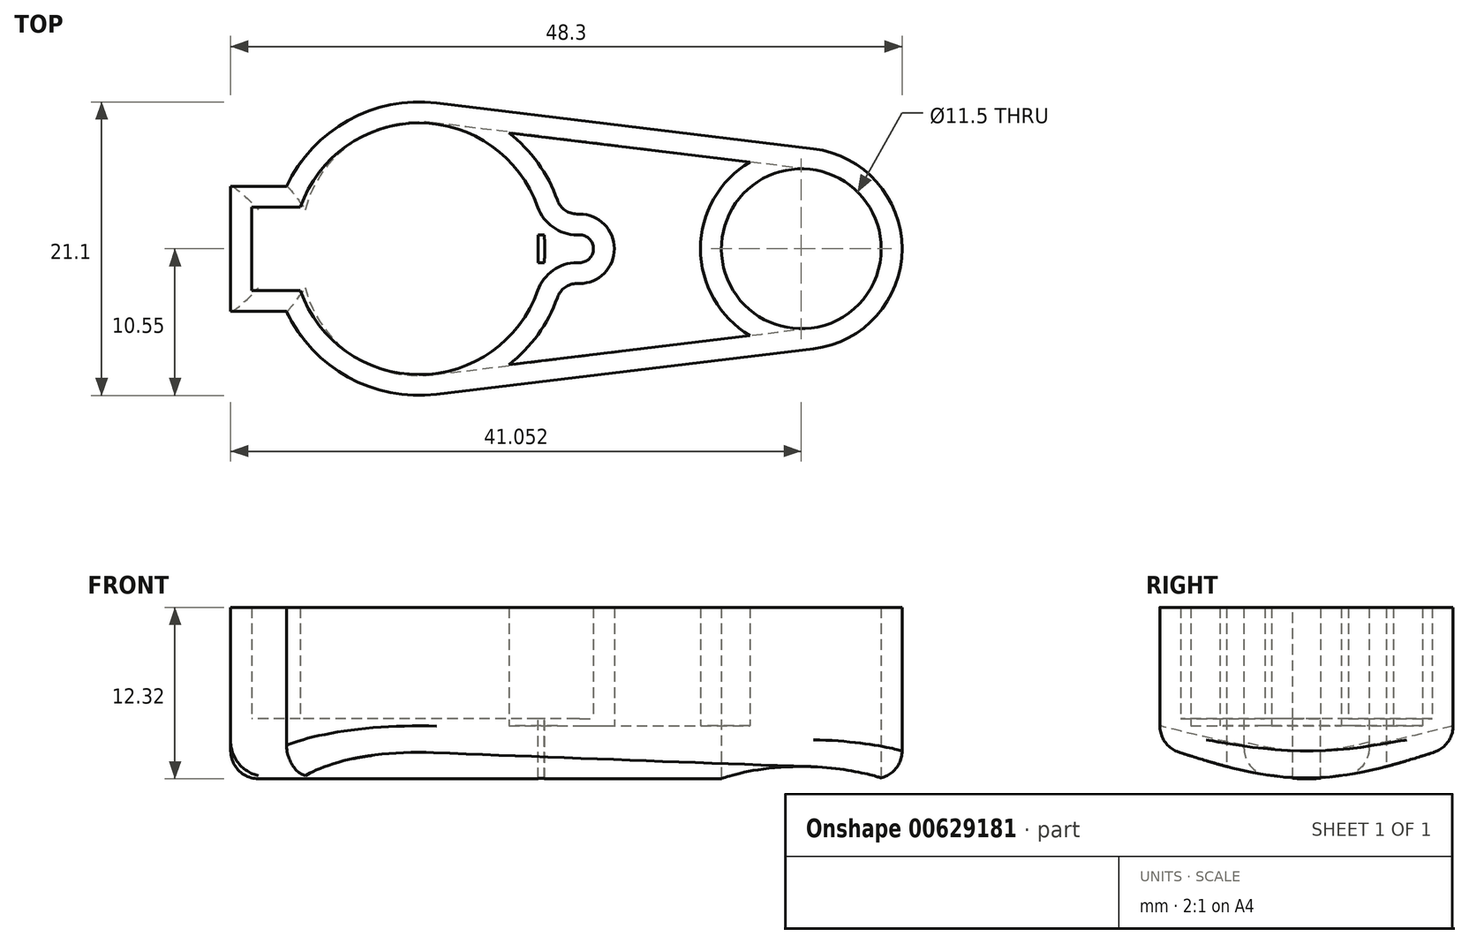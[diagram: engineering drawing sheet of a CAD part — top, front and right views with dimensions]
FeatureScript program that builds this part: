
annotation { "Feature Type Name" : "Feature", "Feature Type Description" : "" }
export const myFeature = defineFeature(function(context is Context, id is Id, definition is map)
    precondition{}
    {
        {
            var Q0;
            Q0=qCreatedBy(makeId("Top.planeOp"),FACE);
            var sketch = newSketch(context, id + "F0", { "sketchPlane" : qUnion([Q0])});
            skCircle(sketch, "E0", {"center": v(1.2, 0) * mm, "radius": 7.25 * mm});
            skCircle(sketch, "E1", {"center": v(-26.3, 0) * mm, "radius": 10.55 * mm});
            skLineSegment(sketch, "E2", {"start": v(-25.03, 10.47) * mm, "end": v(2.07, 7.2) * mm});
            skLineSegment(sketch, "E3", {"start": v(-25.03, -10.47) * mm, "end": v(2.07, -7.2) * mm});
            skCircle(sketch, "E4", {"center": v(-26.3, 0) * mm, "radius": 9.05 * mm});
            skCircle(sketch, "E5", {"center": v(1.2, 0) * mm, "radius": 5.75 * mm});
            skPoint(sketch, "E6", {"position": v(-35.35, 0) * mm});
            skPoint(sketch, "E7", {"position": v(6.95, 0) * mm});
            skLineSegment(sketch, "E8", {"start": v(-34.84, 3) * mm, "end": v(-34.84, -3) * mm});
            skLineSegment(sketch, "E9.bottom", {"start": v(-34.84, 3) * mm, "end": v(-38.35, 3) * mm});
            skLineSegment(sketch, "E9.top", {"start": v(-34.84, -3) * mm, "end": v(-38.35, -3) * mm});
            skLineSegment(sketch, "E9.right", {"start": v(-38.35, 3) * mm, "end": v(-38.35, -3) * mm});
            skLineSegment(sketch, "E10.0", {"start": v(-35.28, -4.5) * mm, "end": v(-39.85, -4.5) * mm});
            skLineSegment(sketch, "E10.1", {"start": v(-39.85, 4.5) * mm, "end": v(-39.85, -4.5) * mm});
            skLineSegment(sketch, "E10.2", {"start": v(-35.28, 4.5) * mm, "end": v(-39.85, 4.5) * mm});
            skPoint(sketch, "E11", {"position": v(-15.75, 0) * mm});
            skLineSegment(sketch, "E12.bottom", {"start": v(-13.75, 1) * mm, "end": v(-17.75, 1) * mm});
            skLineSegment(sketch, "E12.top", {"start": v(-13.75, -1) * mm, "end": v(-17.75, -1) * mm});
            skLineSegment(sketch, "E12.left", {"start": v(-13.75, 1) * mm, "end": v(-13.75, -1) * mm});
            skLineSegment(sketch, "E12.right", {"start": v(-17.75, 1) * mm, "end": v(-17.75, -1) * mm});
            skLineSegment(sketch, "E13", {"start": v(-17.3, 1) * mm, "end": v(-17.75, 1) * mm});
            skLineSegment(sketch, "E14", {"start": v(-17.3, -1) * mm, "end": v(-17.75, -1) * mm});
            skSolve(sketch);
        }
        {
            var Q0;
            {var subQ0=sQuery(id+"F0.wireOp",EDGE,"E2");Q0=makeQuery(id+"F0.imprint","IMPRINT",FACE,{"disambiguationData":[TD([[makeQuery(id+"F0.imprint","IMPRINT",EDGE,{"derivedFrom":subQ0}),-1.0]])]});}
            var Q1;
            Q1=makeQuery(id+"F0.imprint","IMPRINT",FACE,{"disambiguationData":[TD([[makeQuery(id+"F0.imprint","IMPRINT",EDGE,{"derivedFrom":sQuery(id+"F0.wireOp",EDGE,"E5")}),-1.0]])]});
            var Q2;
            {var subQ0=sQuery(id+"F0.wireOp",EDGE,"E1");var subQ8=makeQuery(id+"F0.imprint","INTERSECT",VERTEX,{"derivedFrom":[subQ0,sQuery(id+"F0.wireOp",EDGE,"E2")]});Q2=makeQuery(id+"F0.imprint","IMPRINT",FACE,{"disambiguationData":[TD([[makeQuery(id+"F0.imprint","IMPRINT",EDGE,{"disambiguationData":[TD([[subQ8,-1.0]])],"derivedFrom":subQ0}),1.0]])]});}
            var Q3;
            {var subQ0=sQuery(id+"F0.wireOp",EDGE,"E9.right");Q3=makeQuery(id+"F0.imprint","IMPRINT",FACE,{"disambiguationData":[TD([[makeQuery(id+"F0.imprint","IMPRINT",EDGE,{"derivedFrom":subQ0}),-1.0]])]});}
            var Q4;
            {var subQ5=sQuery(id+"F0.wireOp",EDGE,"E1");var subQ9=makeQuery(id+"F0.imprint","INTERSECT",VERTEX,{"derivedFrom":[subQ5,sQuery(id+"F0.wireOp",EDGE,"E10.0")]});Q4=makeQuery(id+"F0.imprint","IMPRINT",FACE,{"disambiguationData":[TD([[makeQuery(id+"F0.imprint","IMPRINT",EDGE,{"disambiguationData":[TD([[subQ9,1.0]])],"derivedFrom":subQ5}),1.0]])]});}
            extrude(context, id + "F1", {"entities" : qUnion([Q0, Q1, Q2, Q3, Q4]), "depth" : 8 * mm, "offsetDistance" : 25 * mm});
        }
        {
            var Q0;
            Q0=makeQuery(id+"F1.opExtrude","SWEPT_EDGE",EDGE,{"disambiguationData":[OSD([sQuery(id+"F0.wireOp",EDGE,"E12.bottom"),sQuery(id+"F0.wireOp",EDGE,"E12.left")])]});
            var Q1;
            Q1=makeQuery(id+"F1.opExtrude","SWEPT_EDGE",EDGE,{"disambiguationData":[OSD([sQuery(id+"F0.wireOp",EDGE,"E12.top"),sQuery(id+"F0.wireOp",EDGE,"E12.left")])]});
            fillet(context, id + "F2", {"entities" : qUnion([Q0, Q1]), "radius" : 1 * mm, "tangentPropagation" : true, "allowEdgeOverflow" : false});
        }
        {
            var Q0;
            Q0=makeQuery(id+"F1.opExtrude","SWEPT_EDGE",EDGE,{"disambiguationData":[OSD([sQuery(id+"F0.wireOp",EDGE,"E4"),sQuery(id+"F0.wireOp",EDGE,"E13")])]});
            var Q1;
            Q1=makeQuery(id+"F1.opExtrude","SWEPT_EDGE",EDGE,{"disambiguationData":[OSD([sQuery(id+"F0.wireOp",EDGE,"E4"),sQuery(id+"F0.wireOp",EDGE,"E14")])]});
            fillet(context, id + "F3", {"entities" : qUnion([Q0, Q1]), "radius" : 3 * mm, "tangentPropagation" : true, "allowEdgeOverflow" : false});
        }
        {
            var Q0;
            Q0=makeQuery(id+"F1.opExtrude","CAP_FACE",FACE,{"disambiguationData":[OSD([sQuery(id+"F0.wireOp",EDGE,"E0"),sQuery(id+"F0.wireOp",EDGE,"E1"),sQuery(id+"F0.wireOp",EDGE,"E2"),sQuery(id+"F0.wireOp",EDGE,"E3"),sQuery(id+"F0.wireOp",EDGE,"E4"),sQuery(id+"F0.wireOp",EDGE,"E5"),sQuery(id+"F0.wireOp",EDGE,"E9.bottom"),sQuery(id+"F0.wireOp",EDGE,"E9.top"),sQuery(id+"F0.wireOp",EDGE,"E9.right"),sQuery(id+"F0.wireOp",EDGE,"E10.0"),sQuery(id+"F0.wireOp",EDGE,"E10.1"),sQuery(id+"F0.wireOp",EDGE,"E10.2"),sQuery(id+"F0.wireOp",EDGE,"E12.bottom"),sQuery(id+"F0.wireOp",EDGE,"E12.top"),sQuery(id+"F0.wireOp",EDGE,"E12.left"),sQuery(id+"F0.wireOp",EDGE,"E13"),sQuery(id+"F0.wireOp",EDGE,"E14")])],"isStart":true});
            var Q1;
            {var subQ3=sQuery(id+"F0.wireOp",EDGE,"E8");Q1=makeQuery(id+"F0.imprint","IMPRINT",FACE,{"disambiguationData":[TD([[makeQuery(id+"F0.imprint","IMPRINT",EDGE,{"derivedFrom":subQ3}),1.0]])]});}
            var Q2;
            {var subQ0=sQuery(id+"F0.wireOp",EDGE,"E9.bottom");var subQ1=sQuery(id+"F0.wireOp",EDGE,"E1");var subQ2=makeQuery(id+"F0.imprint","INTERSECT",VERTEX,{"derivedFrom":[subQ1,subQ0]});Q2=makeQuery(id+"F0.imprint","IMPRINT",FACE,{"disambiguationData":[TD([[makeQuery(id+"F0.imprint","IMPRINT",EDGE,{"disambiguationData":[TD([[subQ2,-1.0]])],"derivedFrom":subQ1}),1.0]])]});}
            var Q3;
            {var subQ5=sQuery(id+"F0.wireOp",EDGE,"E9.right");Q3=makeQuery(id+"F0.imprint","IMPRINT",FACE,{"disambiguationData":[TD([[makeQuery(id+"F0.imprint","IMPRINT",EDGE,{"derivedFrom":subQ5}),1.0]])]});}
            var Q4;
            {var subQ5=sQuery(id+"F0.wireOp",EDGE,"E12.left");Q4=makeQuery(id+"F0.imprint","IMPRINT",FACE,{"disambiguationData":[TD([[makeQuery(id+"F0.imprint","IMPRINT",EDGE,{"derivedFrom":subQ5}),-1.0]])]});}
            var Q5;
            {var subQ1=sQuery(id+"F0.wireOp",EDGE,"E12.bottom");var subQ6=sQuery(id+"F0.wireOp",EDGE,"E1");var subQ8=makeQuery(id+"F0.imprint","INTERSECT",VERTEX,{"derivedFrom":[subQ6,subQ1]});Q5=makeQuery(id+"F0.imprint","IMPRINT",FACE,{"disambiguationData":[TD([[makeQuery(id+"F0.imprint","IMPRINT",EDGE,{"disambiguationData":[TD([[subQ8,1.0]])],"derivedFrom":subQ6}),1.0]])]});}
            var Q6;
            {var subQ3=sQuery(id+"F0.wireOp",EDGE,"E14");Q6=makeQuery(id+"F0.imprint","IMPRINT",FACE,{"disambiguationData":[TD([[makeQuery(id+"F0.imprint","IMPRINT",EDGE,{"derivedFrom":subQ3}),1.0]])]});}
            var Q7;
            {var subQ0=sQuery(id+"F0.wireOp",EDGE,"E8");Q7=makeQuery(id+"F0.imprint","IMPRINT",FACE,{"disambiguationData":[TD([[makeQuery(id+"F0.imprint","IMPRINT",EDGE,{"derivedFrom":subQ0}),-1.0]])]});}
            var Q8;
            {var subQ6=sQuery(id+"F0.wireOp",EDGE,"E13");Q8=makeQuery(id+"F0.imprint","IMPRINT",FACE,{"disambiguationData":[TD([[makeQuery(id+"F0.imprint","IMPRINT",EDGE,{"derivedFrom":subQ6}),-1.0]])]});}
            var Q9;
            {var subQ0=sQuery(id+"F0.wireOp",EDGE,"E14");Q9=makeQuery(id+"F0.imprint","IMPRINT",FACE,{"disambiguationData":[TD([[makeQuery(id+"F0.imprint","IMPRINT",EDGE,{"derivedFrom":subQ0}),-1.0]])]});}
            var Q10;
            {var subQ0=sQuery(id+"F0.wireOp",EDGE,"E13");Q10=makeQuery(id+"F0.imprint","IMPRINT",FACE,{"disambiguationData":[TD([[makeQuery(id+"F0.imprint","IMPRINT",EDGE,{"derivedFrom":subQ0}),1.0]])]});}
            var Q11;
            {var subQ4=sQuery(id+"F0.wireOp",EDGE,"E2");Q11=makeQuery(id+"F0.imprint","IMPRINT",FACE,{"disambiguationData":[TD([[makeQuery(id+"F0.imprint","IMPRINT",EDGE,{"derivedFrom":subQ4}),-1.0]])]});}
            var Q12;
            {var subQ5=sQuery(id+"F0.wireOp",EDGE,"E1");var subQ9=makeQuery(id+"F0.imprint","INTERSECT",VERTEX,{"derivedFrom":[subQ5,sQuery(id+"F0.wireOp",EDGE,"E10.0")]});Q12=makeQuery(id+"F0.imprint","IMPRINT",FACE,{"disambiguationData":[TD([[makeQuery(id+"F0.imprint","IMPRINT",EDGE,{"disambiguationData":[TD([[subQ9,1.0]])],"derivedFrom":subQ5}),1.0]])]});}
            var Q13;
            {var subQ0=sQuery(id+"F0.wireOp",EDGE,"E1");var subQ4=makeQuery(id+"F0.imprint","INTERSECT",VERTEX,{"derivedFrom":[subQ0,sQuery(id+"F0.wireOp",EDGE,"E2")]});Q13=makeQuery(id+"F0.imprint","IMPRINT",FACE,{"disambiguationData":[TD([[makeQuery(id+"F0.imprint","IMPRINT",EDGE,{"disambiguationData":[TD([[subQ4,1.0]])],"derivedFrom":subQ0}),1.0]])]});}
            extrude(context, id + "F4", {"entities" : qUnion([Q0, Q1, Q2, Q3, Q4, Q5, Q6, Q7, Q8, Q9, Q10, Q11, Q12, Q13]), "operationType" : NewBodyOperationType.ADD, "depth" : 2 * mm, "offsetDistance" : 25 * mm});
        }
        {
            var Q0;
            {var subQ0=sQuery(id+"F0.wireOp",EDGE,"E10.1");Q0=makeQuery(id+"F4.boolean.opBoolean","MERGE",FACE,{"derivedFrom":[makeQuery(id+"F1.opExtrude","SWEPT_FACE",FACE,{"disambiguationData":[OSD([subQ0])]}),makeQuery(id+"F4.opExtrude","SWEPT_FACE",FACE,{"disambiguationData":[OSD([subQ0])]})]});}
            var sketch = newSketch(context, id + "F5", { "sketchPlane" : qUnion([Q0])});
            skPoint(sketch, "E15.0", {"position": v(10.47, -2) * mm});
            skPoint(sketch, "E16.0", {"position": v(-10.47, -2) * mm});
            skPoint(sketch, "E17.1.internal.snap0", {"position": v(0, -2) * mm});
            skFitSpline(sketch, "E17", {"points": [v(10.47, -2) * mm, v(0, -4.32) * mm, v(-10.47, -2) * mm], "startDerivative": vector(-21.92, -6.96) * mm, "endDerivative": vector(-21.92, 6.96) * mm});
            skSolve(sketch);
        }
        {
            var Q0;
            Q0=makeQuery(id+"F1.opExtrude","CAP_FACE",FACE,{"disambiguationData":[OSD([sQuery(id+"F0.wireOp",EDGE,"E0"),sQuery(id+"F0.wireOp",EDGE,"E1"),sQuery(id+"F0.wireOp",EDGE,"E2"),sQuery(id+"F0.wireOp",EDGE,"E3"),sQuery(id+"F0.wireOp",EDGE,"E4"),sQuery(id+"F0.wireOp",EDGE,"E5"),sQuery(id+"F0.wireOp",EDGE,"E9.bottom"),sQuery(id+"F0.wireOp",EDGE,"E9.top"),sQuery(id+"F0.wireOp",EDGE,"E9.right"),sQuery(id+"F0.wireOp",EDGE,"E10.0"),sQuery(id+"F0.wireOp",EDGE,"E10.1"),sQuery(id+"F0.wireOp",EDGE,"E10.2"),sQuery(id+"F0.wireOp",EDGE,"E12.bottom"),sQuery(id+"F0.wireOp",EDGE,"E12.top"),sQuery(id+"F0.wireOp",EDGE,"E12.left"),sQuery(id+"F0.wireOp",EDGE,"E13"),sQuery(id+"F0.wireOp",EDGE,"E14")])],"isStart":false});
            shell(context, id + "F6", {"entities" : qUnion([Q0]), "thickness" : 1.5 * mm});
        }
        {
            var Q0;
            Q0=sQuery(id+"F5.wireOp",EDGE,"E17");
            extrude(context, id + "F7", {"bodyType" : ToolBodyType.SURFACE, "surfaceEntities" : qUnion([Q0]), "oppositeDirection" : true, "depth" : 50 * mm, "offsetDistance" : 25 * mm});
        }
        {
            var Q0;
            {var subQ0=sQuery(id+"F0.wireOp",EDGE,"E9.right");var subQ1=sQuery(id+"F0.wireOp",EDGE,"E9.top");var subQ2=sQuery(id+"F0.wireOp",EDGE,"E9.bottom");var subQ3=sQuery(id+"F0.wireOp",EDGE,"E3");var subQ4=sQuery(id+"F0.wireOp",EDGE,"E2");var subQ5=sQuery(id+"F0.wireOp",EDGE,"E1");var subQ6=sQuery(id+"F0.wireOp",EDGE,"E0");Q0=makeQuery(id+"F4.boolean.opBoolean","MERGE",FACE,{"derivedFrom":[makeQuery(id+"F4.opExtrude","CAP_FACE",FACE,{"disambiguationData":[OSD([subQ6,subQ5,subQ4,subQ3,subQ2,subQ1,subQ0])],"isStart":false}),makeQuery(id+"F4.opExtrude","CAP_FACE",FACE,{"disambiguationData":[OSD([subQ6,subQ5,subQ4,subQ3,sQuery(id+"F0.wireOp",EDGE,"E4"),sQuery(id+"F0.wireOp",EDGE,"E5"),subQ2,subQ1,subQ0,sQuery(id+"F0.wireOp",EDGE,"E10.0"),sQuery(id+"F0.wireOp",EDGE,"E10.1"),sQuery(id+"F0.wireOp",EDGE,"E10.2"),sQuery(id+"F0.wireOp",EDGE,"E12.bottom"),sQuery(id+"F0.wireOp",EDGE,"E12.top"),sQuery(id+"F0.wireOp",EDGE,"E12.left"),sQuery(id+"F0.wireOp",EDGE,"E13"),sQuery(id+"F0.wireOp",EDGE,"E14")])],"isStart":false})]});}
            var Q1;
            Q1=makeQuery(id+"F7.opExtrude","SWEPT_FACE",FACE,{"disambiguationData":[OSD([sQuery(id+"F5.wireOp",EDGE,"E17")])]});
            extrude(context, id + "F8", {"entities" : qUnion([Q0]), "operationType" : NewBodyOperationType.ADD, "endBound" : BoundingType.UP_TO_SURFACE, "depth" : 25 * mm, "endBoundEntityFace" : qUnion([Q1]), "offsetDistance" : 25 * mm});
        }
        {
            var Q0;
            {var subQ0=sQuery(id+"F0.wireOp",EDGE,"E1");var subQ1=makeQuery(id+"F0.imprint","INTERSECT",VERTEX,{"derivedFrom":[subQ0,sQuery(id+"F0.wireOp",EDGE,"E10.0")]});Q0=makeQuery(id+"F8.opExtrude","CAP_EDGE",EDGE,{"disambiguationData":[OSD([subQ0]),TDD([makeQuery(id+"F4.opExtrude","CAP_EDGE",EDGE,{"disambiguationData":[OSD([subQ0]),TDD([makeQuery(id+"F0.imprint","IMPRINT",EDGE,{"disambiguationData":[TD([[subQ1,1.0]])],"derivedFrom":subQ0}),makeQuery(id+"F0.imprint","IMPRINT",EDGE,{"disambiguationData":[TD([[makeQuery(id+"F0.imprint","INTERSECT",VERTEX,{"derivedFrom":[subQ0,sQuery(id+"F0.wireOp",EDGE,"E3")]}),1.0]])],"derivedFrom":subQ0})])],"isStart":false})])],"isStart":false});}
            var Q1;
            {var subQ0=sQuery(id+"F0.wireOp",EDGE,"E3");Q1=makeQuery(id+"F8.opExtrude","TWEAK_EDGE",EDGE,{"derivedFrom":[makeQuery(id+"F4.opExtrude","CAP_EDGE",EDGE,{"disambiguationData":[OSD([subQ0]),TDD([makeQuery(id+"F0.imprint","IMPRINT",EDGE,{"derivedFrom":subQ0})])],"isStart":false}),makeQuery(id+"F7.opExtrude","SWEPT_FACE",FACE,{"disambiguationData":[OSD([sQuery(id+"F5.wireOp",EDGE,"E17")])]})]});}
            var Q2;
            Q2=makeQuery(id+"F8.opExtrude","CAP_EDGE",EDGE,{"disambiguationData":[OSD([sQuery(id+"F0.wireOp",EDGE,"E10.0")])],"isStart":false});
            var Q3;
            Q3=makeQuery(id+"F8.opExtrude","CAP_EDGE",EDGE,{"disambiguationData":[OSD([sQuery(id+"F0.wireOp",EDGE,"E10.1")])],"isStart":false});
            var Q4;
            Q4=makeQuery(id+"F8.opExtrude","CAP_EDGE",EDGE,{"disambiguationData":[OSD([sQuery(id+"F0.wireOp",EDGE,"E10.2")])],"isStart":false});
            var Q5;
            {var subQ0=sQuery(id+"F0.wireOp",EDGE,"E1");var subQ1=makeQuery(id+"F0.imprint","INTERSECT",VERTEX,{"derivedFrom":[subQ0,sQuery(id+"F0.wireOp",EDGE,"E10.2")]});Q5=makeQuery(id+"F8.opExtrude","CAP_EDGE",EDGE,{"disambiguationData":[OSD([subQ0]),TDD([makeQuery(id+"F4.opExtrude","CAP_EDGE",EDGE,{"disambiguationData":[OSD([subQ0]),TDD([makeQuery(id+"F0.imprint","IMPRINT",EDGE,{"disambiguationData":[TD([[makeQuery(id+"F0.imprint","INTERSECT",VERTEX,{"derivedFrom":[subQ0,sQuery(id+"F0.wireOp",EDGE,"E2")]}),-1.0]])],"derivedFrom":subQ0}),makeQuery(id+"F0.imprint","IMPRINT",EDGE,{"disambiguationData":[TD([[subQ1,-1.0]])],"derivedFrom":subQ0})])],"isStart":false})])],"isStart":false});}
            var Q6;
            {var subQ0=sQuery(id+"F0.wireOp",EDGE,"E1");var subQ1=makeQuery(id+"F0.imprint","INTERSECT",VERTEX,{"derivedFrom":[subQ0,sQuery(id+"F0.wireOp",EDGE,"E10.0")]});Q6=makeQuery(id+"F4.opExtrude","CAP_EDGE",EDGE,{"disambiguationData":[OSD([subQ0]),TDD([makeQuery(id+"F0.imprint","IMPRINT",EDGE,{"disambiguationData":[TD([[subQ1,1.0]])],"derivedFrom":subQ0}),makeQuery(id+"F0.imprint","IMPRINT",EDGE,{"disambiguationData":[TD([[makeQuery(id+"F0.imprint","INTERSECT",VERTEX,{"derivedFrom":[subQ0,sQuery(id+"F0.wireOp",EDGE,"E3")]}),1.0]])],"derivedFrom":subQ0})])],"isStart":false});}
            var Q7;
            {var subQ0=sQuery(id+"F0.wireOp",EDGE,"E2");Q7=makeQuery(id+"F8.opExtrude","TWEAK_EDGE",EDGE,{"derivedFrom":[makeQuery(id+"F4.opExtrude","CAP_EDGE",EDGE,{"disambiguationData":[OSD([subQ0]),TDD([makeQuery(id+"F0.imprint","IMPRINT",EDGE,{"derivedFrom":subQ0})])],"isStart":false}),makeQuery(id+"F7.opExtrude","SWEPT_FACE",FACE,{"disambiguationData":[OSD([sQuery(id+"F5.wireOp",EDGE,"E17")])]})]});}
            var Q8;
            {var subQ0=sQuery(id+"F0.wireOp",EDGE,"E1");var subQ1=makeQuery(id+"F0.imprint","INTERSECT",VERTEX,{"derivedFrom":[subQ0,sQuery(id+"F0.wireOp",EDGE,"E10.2")]});Q8=makeQuery(id+"F4.opExtrude","CAP_EDGE",EDGE,{"disambiguationData":[OSD([subQ0]),TDD([makeQuery(id+"F0.imprint","IMPRINT",EDGE,{"disambiguationData":[TD([[makeQuery(id+"F0.imprint","INTERSECT",VERTEX,{"derivedFrom":[subQ0,sQuery(id+"F0.wireOp",EDGE,"E2")]}),-1.0]])],"derivedFrom":subQ0}),makeQuery(id+"F0.imprint","IMPRINT",EDGE,{"disambiguationData":[TD([[subQ1,-1.0]])],"derivedFrom":subQ0})])],"isStart":false});}
            fillet(context, id + "F9", {"entities" : qUnion([Q0, Q1, Q2, Q3, Q4, Q5, Q6, Q7, Q8]), "radius" : 2 * mm, "tangentPropagation" : true, "allowEdgeOverflow" : false});
        }
    });
